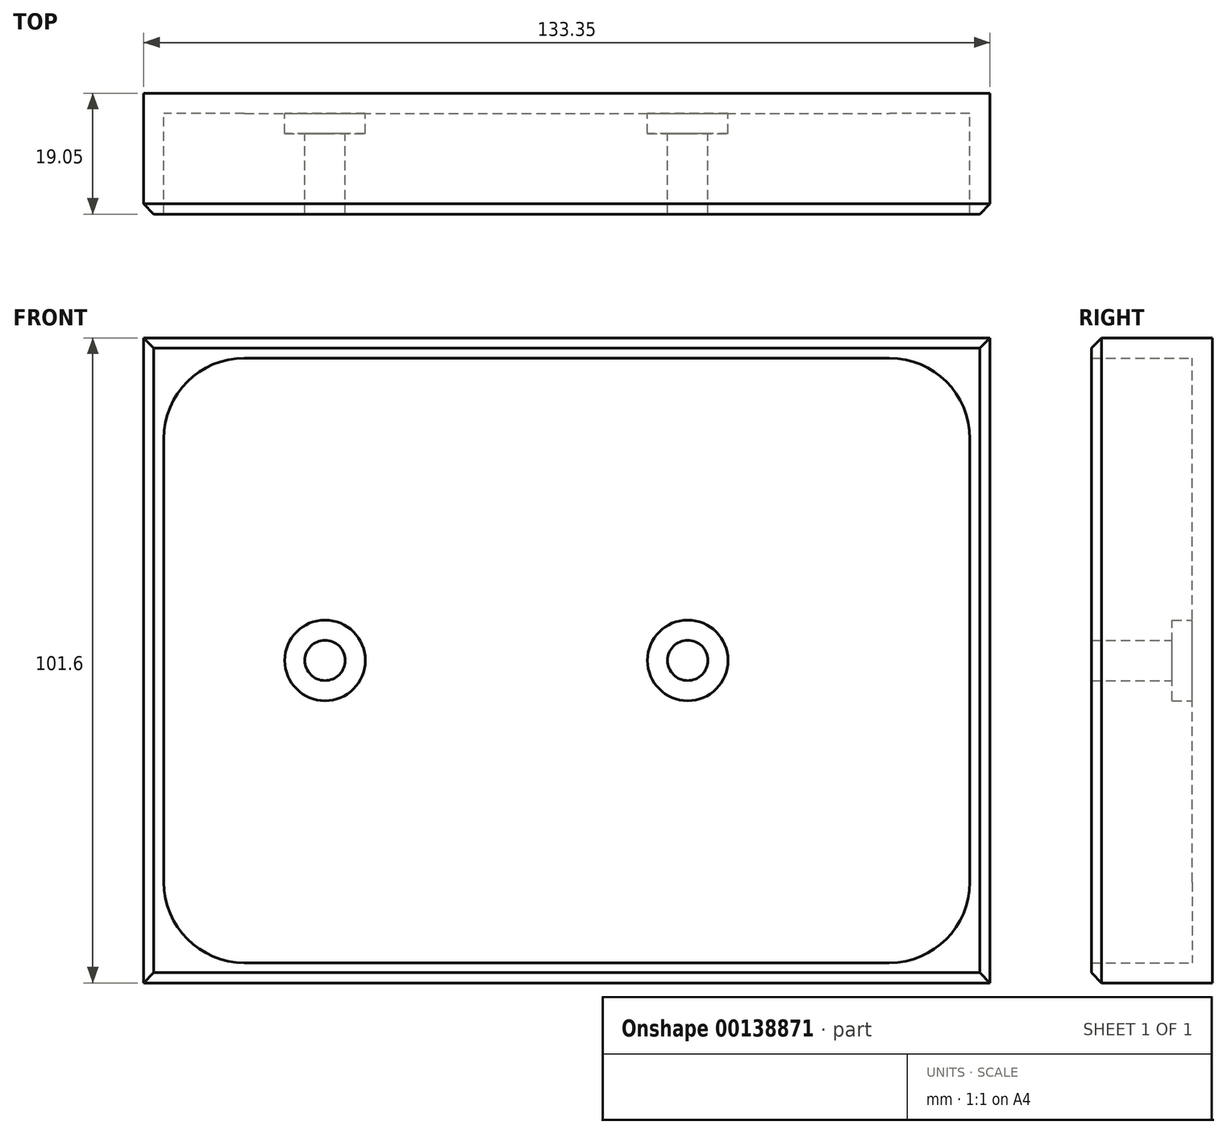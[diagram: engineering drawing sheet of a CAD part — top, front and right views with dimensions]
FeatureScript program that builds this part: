
annotation { "Feature Type Name" : "Feature", "Feature Type Description" : "" }
export const myFeature = defineFeature(function(context is Context, id is Id, definition is map)
    precondition{}
    {
        {
            var Q0;
            Q0=qCreatedBy(makeId("Front.planeOp"),FACE);
            var sketch = newSketch(context, id + "F0", { "sketchPlane" : qUnion([Q0])});
            skLineSegment(sketch, "E0.bottom", {"start": v(0, 0) * mm, "end": v(133.35, 0) * mm});
            skLineSegment(sketch, "E0.top", {"start": v(0, 101.6) * mm, "end": v(133.35, 101.6) * mm});
            skLineSegment(sketch, "E0.left", {"start": v(0, 0) * mm, "end": v(0, 101.6) * mm});
            skLineSegment(sketch, "E0.right", {"start": v(133.35, 0) * mm, "end": v(133.35, 101.6) * mm});
            skSolve(sketch);
        }
        {
            var Q0;
            Q0 = qSketchRegion(id + "F0", true);
            extrude(context, id + "F1", {"entities" : qUnion([Q0]), "depth" : 19.05 * mm});
        }
        {
            var Q0;
            Q0=makeQuery(id+"F1.opExtrude","CAP_FACE",FACE,{"disambiguationData":[OSD([sQuery(id+"F0.wireOp",EDGE,"E0.bottom"),sQuery(id+"F0.wireOp",EDGE,"E0.top"),sQuery(id+"F0.wireOp",EDGE,"E0.left"),sQuery(id+"F0.wireOp",EDGE,"E0.right")])],"isStart":false});
            shell(context, id + "F2", {"entities" : qUnion([Q0]), "thickness" : 3.17 * mm});
        }
        {
            var Q0;
            Q0=makeQuery(id+"F2.opShell","OFFSET_FACE",FACE,{"disambiguationData":[OSD([sQuery(id+"F0.wireOp",EDGE,"E0.bottom"),sQuery(id+"F0.wireOp",EDGE,"E0.top"),sQuery(id+"F0.wireOp",EDGE,"E0.left"),sQuery(id+"F0.wireOp",EDGE,"E0.right")])]});
            var sketch = newSketch(context, id + "F3", { "sketchPlane" : qUnion([Q0])});
            skCircle(sketch, "E1", {"center": v(28.58, 50.8) * mm, "radius": 6.35 * mm});
            skPoint(sketch, "E1.centerSnap0", {"position": v(3.17, 50.8) * mm});
            skCircle(sketch, "E2", {"center": v(85.73, 50.8) * mm, "radius": 6.35 * mm});
            skSolve(sketch);
        }
        {
            var Q0;
            Q0 = qSketchRegion(id + "F3", true);
            extrude(context, id + "F4", {"entities" : qUnion([Q0]), "operationType" : NewBodyOperationType.ADD, "depth" : 3.17 * mm});
        }
        {
            var Q0;
            Q0=makeQuery(id+"F4.opExtrude","CAP_FACE",FACE,{"disambiguationData":[OSD([sQuery(id+"F3.wireOp",EDGE,"E1")])],"isStart":false});
            var sketch = newSketch(context, id + "F5", { "sketchPlane" : qUnion([Q0])});
            skCircle(sketch, "E3", {"center": v(28.58, 50.8) * mm, "radius": 3.17 * mm});
            skSolve(sketch);
        }
        {
            var Q0;
            Q0 = qSketchRegion(id + "F5", true);
            extrude(context, id + "F6", {"entities" : qUnion([Q0]), "operationType" : NewBodyOperationType.ADD, "depth" : 12.7 * mm});
        }
        {
            var Q0;
            Q0=makeQuery(id+"F4.opExtrude","CAP_FACE",FACE,{"disambiguationData":[OSD([sQuery(id+"F3.wireOp",EDGE,"E2")])],"isStart":false});
            var sketch = newSketch(context, id + "F7", { "sketchPlane" : qUnion([Q0])});
            skCircle(sketch, "E4", {"center": v(85.73, 50.8) * mm, "radius": 3.18 * mm});
            skSolve(sketch);
        }
        {
            var Q0;
            Q0 = qSketchRegion(id + "F7", true);
            extrude(context, id + "F8", {"entities" : qUnion([Q0]), "operationType" : NewBodyOperationType.ADD, "depth" : 12.7 * mm});
        }
        {
            var Q0;
            Q0=makeQuery(id+"F2.opShell","OFFSET_EDGE",EDGE,{"disambiguationData":[OSD([sQuery(id+"F0.wireOp",EDGE,"E0.top"),sQuery(id+"F0.wireOp",EDGE,"E0.left")])]});
            var Q1;
            Q1=makeQuery(id+"F2.opShell","OFFSET_EDGE",EDGE,{"disambiguationData":[OSD([sQuery(id+"F0.wireOp",EDGE,"E0.bottom"),sQuery(id+"F0.wireOp",EDGE,"E0.left")])]});
            var Q2;
            Q2=makeQuery(id+"F2.opShell","OFFSET_EDGE",EDGE,{"disambiguationData":[OSD([sQuery(id+"F0.wireOp",EDGE,"E0.bottom"),sQuery(id+"F0.wireOp",EDGE,"E0.right")])]});
            var Q3;
            Q3=makeQuery(id+"F2.opShell","OFFSET_EDGE",EDGE,{"disambiguationData":[OSD([sQuery(id+"F0.wireOp",EDGE,"E0.top"),sQuery(id+"F0.wireOp",EDGE,"E0.right")])]});
            fillet(context, id + "F9", {"entities" : qUnion([Q0, Q1, Q2, Q3]), "radius" : 12.7 * mm, "tangentPropagation" : true, "allowEdgeOverflow" : false});
        }
        {
            var Q0;
            Q0=makeQuery(id+"F1.opExtrude","CAP_EDGE",EDGE,{"disambiguationData":[OSD([sQuery(id+"F0.wireOp",EDGE,"E0.left")])],"isStart":false});
            var Q1;
            Q1=makeQuery(id+"F1.opExtrude","CAP_EDGE",EDGE,{"disambiguationData":[OSD([sQuery(id+"F0.wireOp",EDGE,"E0.top")])],"isStart":false});
            var Q2;
            Q2=makeQuery(id+"F1.opExtrude","CAP_EDGE",EDGE,{"disambiguationData":[OSD([sQuery(id+"F0.wireOp",EDGE,"E0.right")])],"isStart":false});
            var Q3;
            Q3=makeQuery(id+"F1.opExtrude","CAP_EDGE",EDGE,{"disambiguationData":[OSD([sQuery(id+"F0.wireOp",EDGE,"E0.bottom")])],"isStart":false});
            chamfer(context, id + "F10", {"entities" : qUnion([Q0, Q1, Q2, Q3]), "width" : 1.6 * mm, "tangentPropagation" : true});
        }
    });
